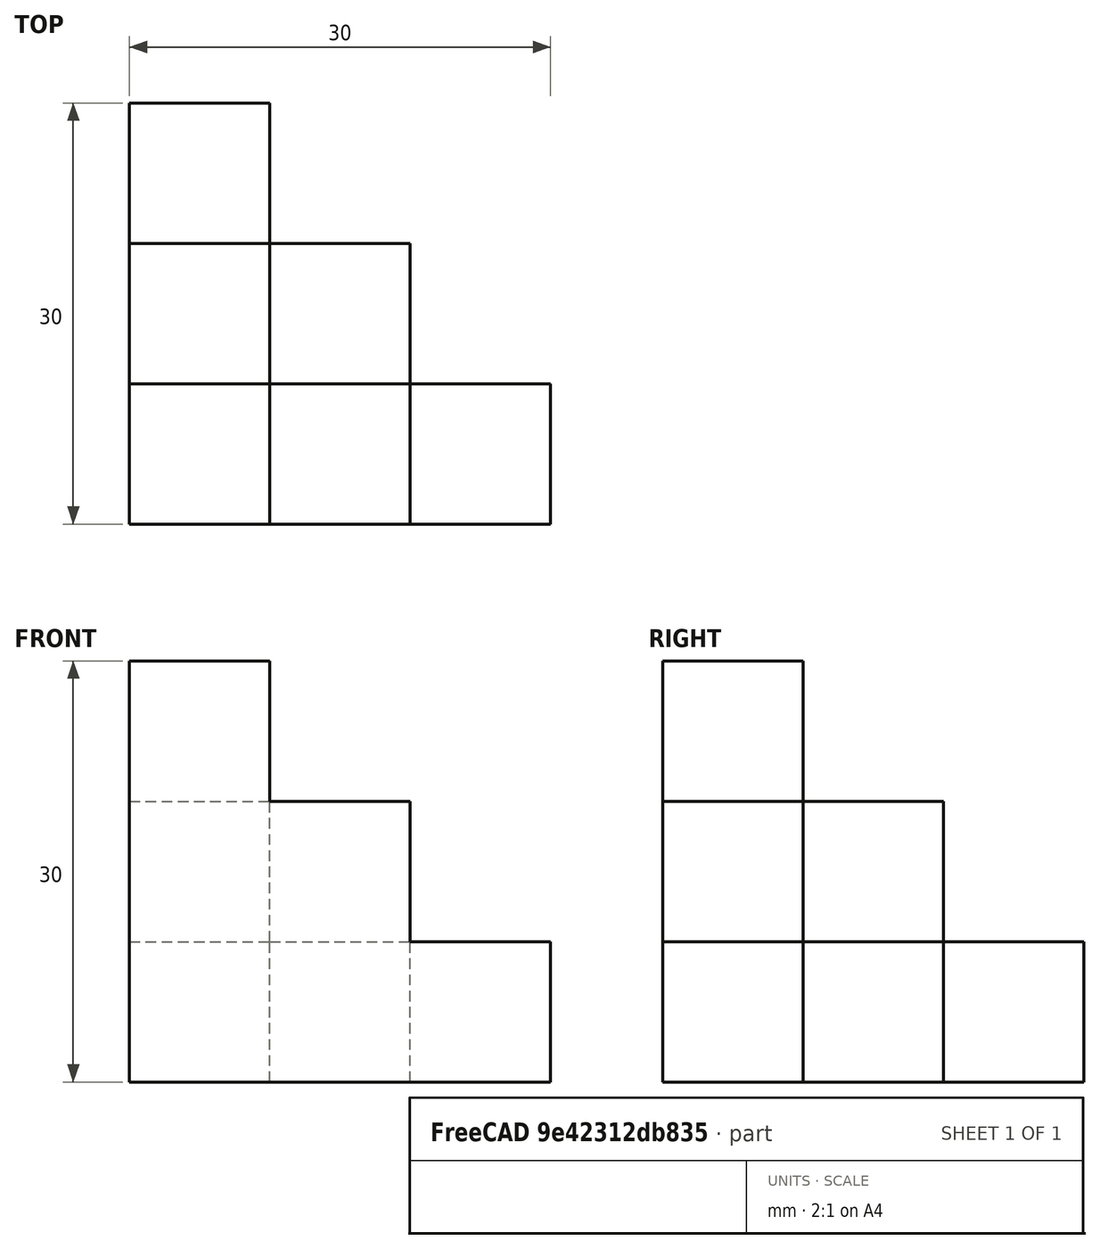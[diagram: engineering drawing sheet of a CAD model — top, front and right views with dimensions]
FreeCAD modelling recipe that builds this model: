
FCSTD DOCUMENT  (FreeCAD 0.21R33771 (Git))
Label: OJT1_T05R02_unions_qubert3
License: All rights reserved
LicenseURL: https://en.wikipedia.org/wiki/All_rights_reserved
objects: Part::Box×6, Part::MultiFuse×1
note: 7 computed .brp shape members not serialized (recipe doc carries the construction recipe); baked Part::Feature solids carry a one-line shape summary decoded from their .brp

FEATURE [Part::Box] Box  label="Cube"
  AttacherType = Attacher::AttachEngine3D
  Height = 30
  Length = 10
  Width = 10
FEATURE [Part::Box] Box001  label="Cube001"
  AttacherType = Attacher::AttachEngine3D
  Height = 20
  Length = 10
  Placement = pos=(10,0,0) rot=(0,0,1;0rad)
  Width = 10
FEATURE [Part::Box] Box002  label="Cube002"
  AttacherType = Attacher::AttachEngine3D
  Height = 20
  Length = 10
  Placement = pos=(0,10,0) rot=(0,0,1;0rad)
  Width = 10
FEATURE [Part::Box] Box003  label="Cube003"
  AttacherType = Attacher::AttachEngine3D
  Height = 10
  Length = 10
  Placement = pos=(20,0,0) rot=(0,0,1;0rad)
  Width = 10
FEATURE [Part::Box] Box004  label="Cube004"
  AttacherType = Attacher::AttachEngine3D
  Height = 10
  Length = 10
  Placement = pos=(0,20,0) rot=(0,0,1;0rad)
  Width = 10
FEATURE [Part::Box] Box005  label="Cube005"
  AttacherType = Attacher::AttachEngine3D
  Height = 10
  Length = 10
  Placement = pos=(10,10,0) rot=(0,0,1;0rad)
  Width = 10
FEATURE [Part::MultiFuse] Fusion
  Refine = true
  Shapes = -> [Box005,Box,Box001,Box002,Box003,Box004]
